# Revit family: SJS
name_source: partatom
category: Specialty Equipment
units: mm (PartAtom-declared; Revit-internal decimal feet)

## family parameters
Cut with Voids When Loaded = No
Host = Face
Part Type = Normal
Room Calculation Point = No
Round Connector Dimension = Use Diameter
Shared = No

## types (19) — shared parameters
ABAA Compliance = Yes
Assembly Code = C3020200
Coverplate Material = Aluminum
Default Elevation = 0"
Description = Watertight, Sound Dampening, Primary Seal for Interior and Exterior Deck and Floor Expansion Joints
Durometer Hardness of Silicone Coating (ASTM D2240) = Shore A: 30
Manufacturer = EMSEAL Joint Systems Ltd
Manufacturer URL = http://www.emseal.com
Model = SJS
Movement (of Nominal Material Size) = +50% / -50%
Product Data URL = https://bit.ly
Product Documentataion URL = https://bit.ly
Product Page URL = https://www.emseal.com
R Value Range (ASTM C518) = 18 per 1-inch (25mm) depth
Rate of Air Leakage (ASTM E283) = Passed
Seal Material = Silicone - Sikasil WS-295 Deck Gray
Seal Material Note = SJS is coated on the top with Sikasil WS-295 silicone.
Staining (ASTM C510) = None
Temperature Range (ASTM C711) = 185°F (85°C) to -40°F (-40°C)
Tensile Strength (ASTM D3574) = 21 psi min; 145 kPa
Type Image = SJS.png

## per-type parameters (varying)
| type | Coverplate Width | Depth | Double Bellow 3 inches | Double Bellow 4 inches | Hex Bellow 5 inches | Narrow Spline ON | Nono Bellow 5 inches | Octo Bellow 5 inches | Quad Bellow 4 inches | Quint Bellow 5 inches | Sept Bellow 5 inches | Spline ON | Spline Width | Triple Bellow 3 inches | Triple Bellow 4 inches | Width |
| SJS - 2 inches | 6" | 3" | Yes | No | No | Yes | No | No | No | No | No | No | 3/8" | No | No | 2" |
| SJS - 2.5 inches | 6 3/4" | 3" | Yes | No | No | Yes | No | No | No | No | No | No | 3/8" | No | No | 2 1/2" |
| SJS - 3 inches | 7 1/2" | 3" | No | No | No | Yes | No | No | No | No | No | No | 3/8" | Yes | No | 3" |
| SJS - 3.5 inches | 8 1/4" | 3" | No | No | No | Yes | No | No | No | No | No | No | 3/8" | Yes | No | 3 1/2" |
| SJS - 4 inches | 9" | 4" | No | Yes | No | No | No | No | No | No | No | Yes | 3/4" | No | No | 4" |
| SJS - 5 inches | 10 1/2" | 4" | No | Yes | No | No | No | No | No | No | No | Yes | 3/4" | No | No | 5" |
| SJS - 6 inches | 1' - 0" | 4" | No | No | No | No | No | No | No | No | No | Yes | 3/4" | No | Yes | 6" |
| SJS - 7 inches | 1' - 1 1/2" | 4" | No | No | No | No | No | No | No | No | No | Yes | 3/4" | No | Yes | 7" |
| SJS - 8 inches | 1' - 3" | 4" | No | No | No | No | No | No | Yes | No | No | Yes | 3/4" | No | No | 8" |
| SJS - 9 inches | 1' - 4 1/2" | 5" | No | No | No | No | No | No | Yes | No | No | Yes | 3/4" | No | No | 9" |
| SJS - 10 inches | 1' - 6" | 5" | No | No | No | No | No | No | No | Yes | No | Yes | 3/4" | No | No | 10" |
| SJS - 11 inches | 1' - 7 1/2" | 5" | No | No | No | No | No | No | No | Yes | No | Yes | 3/4" | No | No | 11" |
| SJS - 12 inches | 1' - 9" | 5" | No | No | Yes | No | No | No | No | No | No | Yes | 3/4" | No | No | 1' - 0" |
| SJS - 13 inches | 1' - 10 1/2" | 5" | No | No | Yes | No | No | No | No | No | No | Yes | 3/4" | No | No | 1' - 1" |
| SJS - 14 inches | 2' - 0" | 5" | No | No | No | No | No | No | No | No | Yes | Yes | 3/4" | No | No | 1' - 2" |
| SJS - 15 inches | 2' - 1 1/2" | 5" | No | No | No | No | No | No | No | No | Yes | Yes | 3/4" | No | No | 1' - 3" |
| SJS - 16 inches | 2' - 3" | 5" | No | No | No | No | No | Yes | No | No | No | Yes | 3/4" | No | No | 1' - 4" |
| SJS - 17 inches | 2' - 4 1/2" | 5" | No | No | No | No | No | Yes | No | No | No | Yes | 3/4" | No | No | 1' - 5" |
| SJS - 18 inches | 2' - 6" | 5" | No | No | No | No | Yes | No | No | No | No | Yes | 3/4" | No | No | 1' - 6" |

## geometry (parser evidence)
native form markers: Sweep x2
no freeform markers — native parametric forms only
